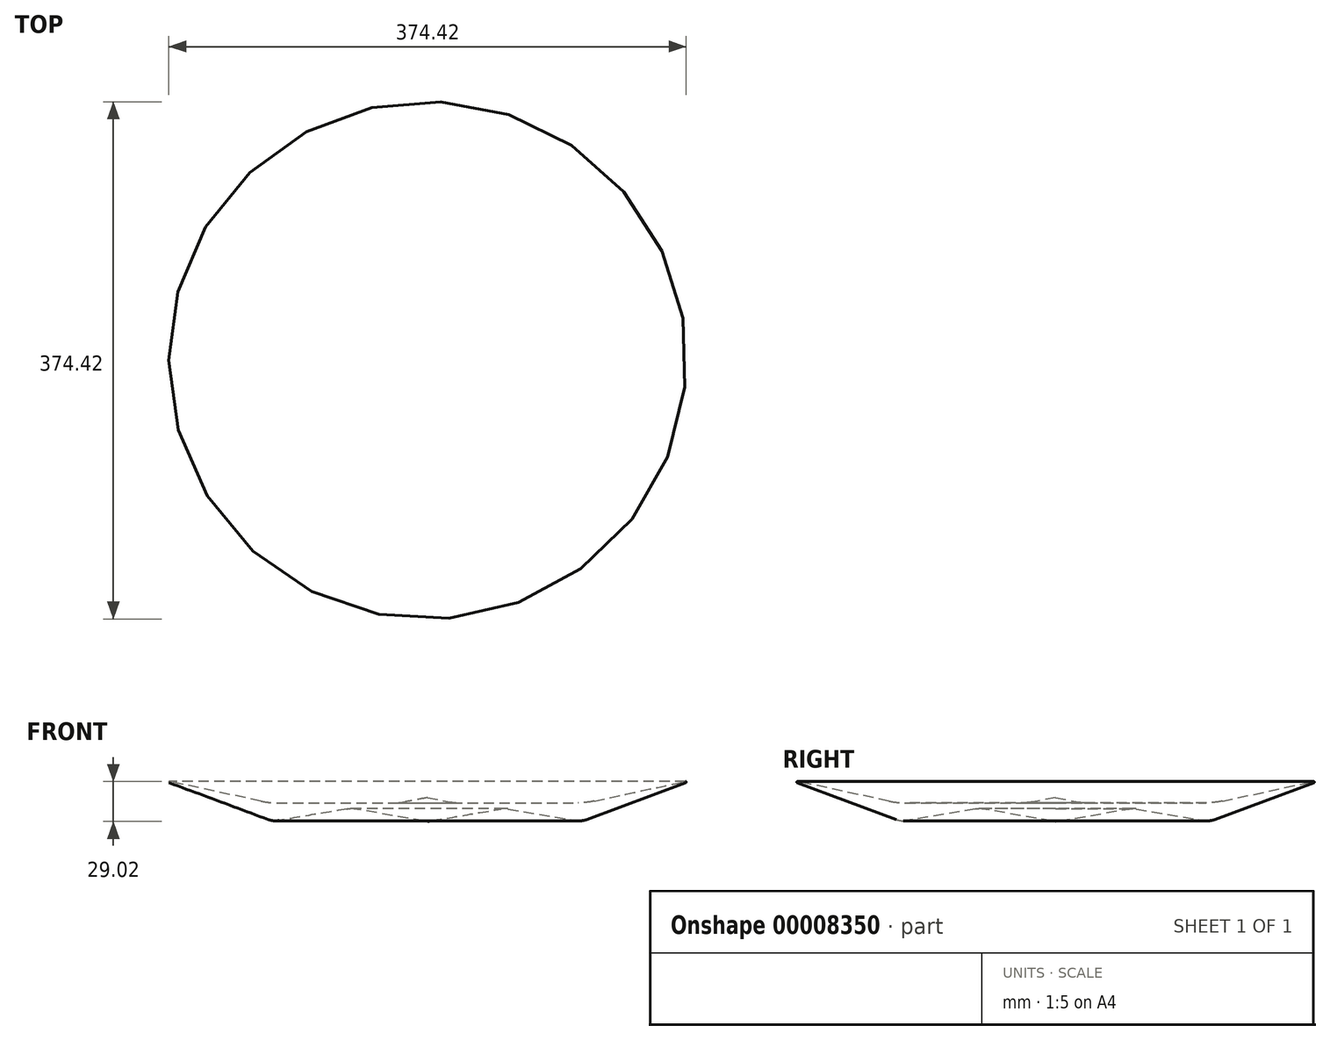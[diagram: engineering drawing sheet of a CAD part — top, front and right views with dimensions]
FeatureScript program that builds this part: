
annotation { "Feature Type Name" : "Feature", "Feature Type Description" : "" }
export const myFeature = defineFeature(function(context is Context, id is Id, definition is map)
    precondition{}
    {
        {
            var Q0;
            Q0=qCreatedBy(makeId("Front.planeOp"),FACE);
            var sketch = newSketch(context, id + "F0", { "sketchPlane" : qUnion([Q0])});
            skLineSegment(sketch, "E0", {"start": v(0, 0) * mm, "end": v(55.74, 9.54) * mm});
            skLineSegment(sketch, "E1", {"start": v(55.74, 9.54) * mm, "end": v(111.48, 0) * mm});
            skLineSegment(sketch, "E2", {"start": v(111.48, 0) * mm, "end": v(193.4, 30.48) * mm});
            skLineSegment(sketch, "E3", {"start": v(193.4, 30.48) * mm, "end": v(114.84, 13.5) * mm});
            skLineSegment(sketch, "E4", {"start": v(114.84, 13.5) * mm, "end": v(19.81, 13.5) * mm});
            skLineSegment(sketch, "E5", {"start": v(19.81, 13.5) * mm, "end": v(0, 17.3) * mm});
            skLineSegment(sketch, "E6", {"start": v(0, 17.3) * mm, "end": v(0, 0) * mm});
            skSolve(sketch);
        }
        {
            var Q0;
            Q0 = qSketchRegion(id + "F0", true);
            var Q1;
            Q1=sQuery(id+"F0.wireOp",EDGE,"E6");
            revolve(context, id + "F1", {"entities" : qUnion([Q0]), "axis" : qUnion([Q1]), "revolveType" : RevolveType.FULL});
        }
        {
            var Q0;
            Q0=makeQuery(id+"F1.opRevolve","SWEPT_EDGE",EDGE,{"disambiguationData":[OSD([sQuery(id+"F0.wireOp",EDGE,"E4"),sQuery(id+"F0.wireOp",EDGE,"E5")])]});
            fillet(context, id + "F2", {"entities" : qUnion([Q0]), "radius" : 35 * mm, "tangentPropagation" : true, "allowEdgeOverflow" : false});
        }
        {
            var Q0;
            Q0=makeQuery(id+"F1.opRevolve","SWEPT_EDGE",EDGE,{"disambiguationData":[OSD([sQuery(id+"F0.wireOp",EDGE,"E3"),sQuery(id+"F0.wireOp",EDGE,"E4")])]});
            fillet(context, id + "F3", {"entities" : qUnion([Q0]), "radius" : 55 * mm, "tangentPropagation" : true, "allowEdgeOverflow" : false});
        }
        {
            var Q0;
            Q0=makeQuery(id+"F1.opRevolve","SWEPT_EDGE",EDGE,{"disambiguationData":[OSD([sQuery(id+"F0.wireOp",EDGE,"E2"),sQuery(id+"F0.wireOp",EDGE,"E3")])]});
            fillet(context, id + "F4", {"entities" : qUnion([Q0]), "radius" : 0.5 * mm, "tangentPropagation" : true, "allowEdgeOverflow" : false});
        }
        {
            var Q0;
            Q0=makeQuery(id+"F1.opRevolve","SWEPT_EDGE",EDGE,{"disambiguationData":[OSD([sQuery(id+"F0.wireOp",EDGE,"E1"),sQuery(id+"F0.wireOp",EDGE,"E2")])]});
            fillet(context, id + "F5", {"entities" : qUnion([Q0]), "radius" : 15 * mm, "allowEdgeOverflow" : false});
        }
        {
            var Q0;
            Q0=makeQuery(id+"F1.opRevolve","SWEPT_EDGE",EDGE,{"disambiguationData":[OSD([sQuery(id+"F0.wireOp",EDGE,"E0"),sQuery(id+"F0.wireOp",EDGE,"E1")])]});
            fillet(context, id + "F6", {"entities" : qUnion([Q0]), "radius" : 15 * mm, "tangentPropagation" : true, "allowEdgeOverflow" : false});
        }
    });
